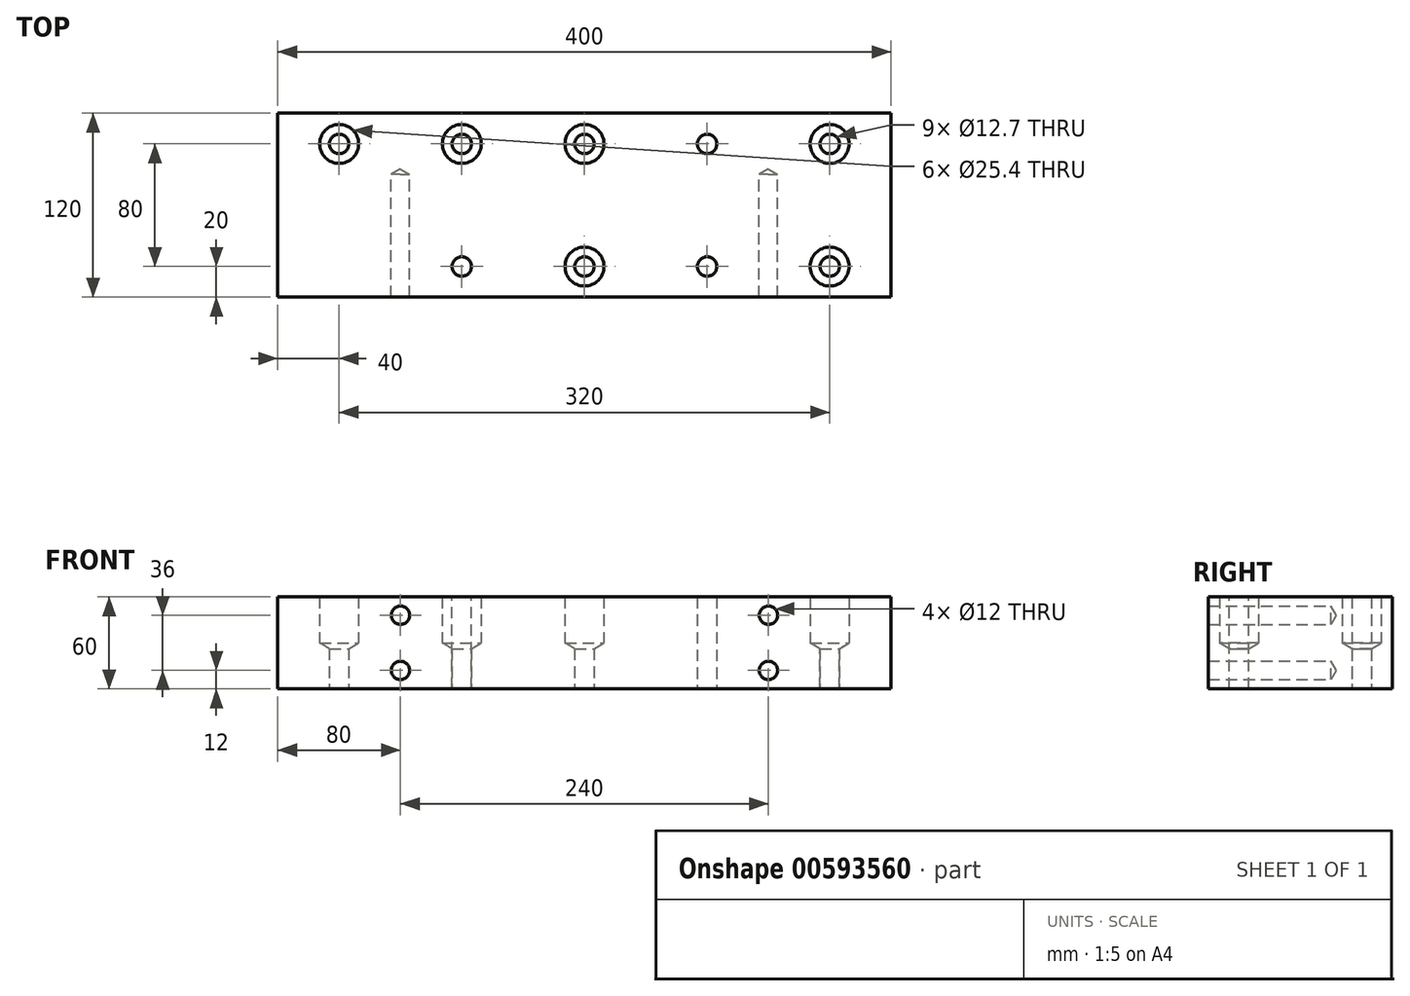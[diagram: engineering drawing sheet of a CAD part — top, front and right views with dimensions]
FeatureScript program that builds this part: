
annotation { "Feature Type Name" : "Feature", "Feature Type Description" : "" }
export const myFeature = defineFeature(function(context is Context, id is Id, definition is map)
    precondition{}
    {
        {
            var Q0;
            Q0=qCreatedBy(makeId("Top.planeOp"),FACE);
            var sketch = newSketch(context, id + "F0", { "sketchPlane" : qUnion([Q0])});
            skLineSegment(sketch, "E0.bottom", {"start": v(-200, 120) * mm, "end": v(200, 120) * mm});
            skLineSegment(sketch, "E0.top", {"start": v(-200, 0) * mm, "end": v(200, 0) * mm});
            skLineSegment(sketch, "E0.left", {"start": v(-200, 120) * mm, "end": v(-200, 0) * mm});
            skLineSegment(sketch, "E0.right", {"start": v(200, 120) * mm, "end": v(200, 0) * mm});
            skCircle(sketch, "E1.MirrorC", {"center": v(160, 20) * mm, "radius": 12.7 * mm});
            skCircle(sketch, "E2.MirrorC", {"center": v(80, 20) * mm, "radius": 12.7 * mm});
            skCircle(sketch, "E3.MirrorC", {"center": v(0, 20) * mm, "radius": 6.35 * mm});
            skCircle(sketch, "E4.MirrorC", {"center": v(-80, 20) * mm, "radius": 12.7 * mm});
            skCircle(sketch, "E5.MirrorC", {"center": v(-80, 20) * mm, "radius": 6.35 * mm});
            skCircle(sketch, "E6.MirrorC", {"center": v(0, 20) * mm, "radius": 12.7 * mm});
            skCircle(sketch, "E7.MirrorC", {"center": v(160, 20) * mm, "radius": 6.35 * mm});
            skCircle(sketch, "E8.MirrorC", {"center": v(80, 20) * mm, "radius": 6.35 * mm});
            skCircle(sketch, "E9.MirrorC", {"center": v(160, 100) * mm, "radius": 6.35 * mm});
            skCircle(sketch, "E10.MirrorC", {"center": v(160, 100) * mm, "radius": 12.7 * mm});
            skCircle(sketch, "E11.MirrorC", {"center": v(-160, 100) * mm, "radius": 6.35 * mm});
            skCircle(sketch, "E12.MirrorC", {"center": v(80, 100) * mm, "radius": 12.7 * mm});
            skCircle(sketch, "E13.MirrorC", {"center": v(80, 100) * mm, "radius": 6.35 * mm});
            skCircle(sketch, "E14.MirrorC", {"center": v(0, 100) * mm, "radius": 6.35 * mm});
            skCircle(sketch, "E15.MirrorC", {"center": v(-80, 100) * mm, "radius": 6.35 * mm});
            skCircle(sketch, "E16.MirrorC", {"center": v(0, 100) * mm, "radius": 12.7 * mm});
            skCircle(sketch, "E17.MirrorC", {"center": v(-80, 100) * mm, "radius": 12.7 * mm});
            skCircle(sketch, "E18.MirrorC", {"center": v(-160, 100) * mm, "radius": 12.7 * mm});
            skSolve(sketch);
        }
        {
            var Q0;
            Q0=makeQuery(id+"F0.imprint","IMPRINT",FACE,{"disambiguationData":[TD([[makeQuery(id+"F0.imprint","IMPRINT",EDGE,{"derivedFrom":sQuery(id+"F0.wireOp",EDGE,"E0.bottom")}),-1.0]])]});
            var Q1;
            Q1=makeQuery(id+"F0.imprint","IMPRINT",FACE,{"disambiguationData":[TD([[makeQuery(id+"F0.imprint","IMPRINT",EDGE,{"derivedFrom":sQuery(id+"F0.wireOp",EDGE,"E18.MirrorC")}),1.0]])]});
            var Q2;
            Q2=makeQuery(id+"F0.imprint","IMPRINT",FACE,{"disambiguationData":[TD([[makeQuery(id+"F0.imprint","IMPRINT",EDGE,{"derivedFrom":sQuery(id+"F0.wireOp",EDGE,"E11.MirrorC")}),1.0]])]});
            var Q3;
            Q3=makeQuery(id+"F0.imprint","IMPRINT",FACE,{"disambiguationData":[TD([[makeQuery(id+"F0.imprint","IMPRINT",EDGE,{"derivedFrom":sQuery(id+"F0.wireOp",EDGE,"E15.MirrorC")}),-1.0]])]});
            var Q4;
            Q4=makeQuery(id+"F0.imprint","IMPRINT",FACE,{"disambiguationData":[TD([[makeQuery(id+"F0.imprint","IMPRINT",EDGE,{"derivedFrom":sQuery(id+"F0.wireOp",EDGE,"E15.MirrorC")}),1.0]])]});
            var Q5;
            Q5=makeQuery(id+"F0.imprint","IMPRINT",FACE,{"disambiguationData":[TD([[makeQuery(id+"F0.imprint","IMPRINT",EDGE,{"derivedFrom":sQuery(id+"F0.wireOp",EDGE,"E14.MirrorC")}),-1.0]])]});
            var Q6;
            Q6=makeQuery(id+"F0.imprint","IMPRINT",FACE,{"disambiguationData":[TD([[makeQuery(id+"F0.imprint","IMPRINT",EDGE,{"derivedFrom":sQuery(id+"F0.wireOp",EDGE,"E14.MirrorC")}),1.0]])]});
            var Q7;
            Q7=makeQuery(id+"F0.imprint","IMPRINT",FACE,{"disambiguationData":[TD([[makeQuery(id+"F0.imprint","IMPRINT",EDGE,{"derivedFrom":sQuery(id+"F0.wireOp",EDGE,"E13.MirrorC")}),1.0]])]});
            var Q8;
            Q8=makeQuery(id+"F0.imprint","IMPRINT",FACE,{"disambiguationData":[TD([[makeQuery(id+"F0.imprint","IMPRINT",EDGE,{"derivedFrom":sQuery(id+"F0.wireOp",EDGE,"E12.MirrorC")}),1.0]])]});
            var Q9;
            Q9=makeQuery(id+"F0.imprint","IMPRINT",FACE,{"disambiguationData":[TD([[makeQuery(id+"F0.imprint","IMPRINT",EDGE,{"derivedFrom":sQuery(id+"F0.wireOp",EDGE,"E9.MirrorC")}),1.0]])]});
            var Q10;
            Q10=makeQuery(id+"F0.imprint","IMPRINT",FACE,{"disambiguationData":[TD([[makeQuery(id+"F0.imprint","IMPRINT",EDGE,{"derivedFrom":sQuery(id+"F0.wireOp",EDGE,"E9.MirrorC")}),-1.0]])]});
            var Q11;
            Q11=makeQuery(id+"F0.imprint","IMPRINT",FACE,{"disambiguationData":[TD([[makeQuery(id+"F0.imprint","IMPRINT",EDGE,{"derivedFrom":sQuery(id+"F0.wireOp",EDGE,"E8.MirrorC")}),-1.0]])]});
            var Q12;
            Q12=makeQuery(id+"F0.imprint","IMPRINT",FACE,{"disambiguationData":[TD([[makeQuery(id+"F0.imprint","IMPRINT",EDGE,{"derivedFrom":sQuery(id+"F0.wireOp",EDGE,"E8.MirrorC")}),1.0]])]});
            var Q13;
            Q13=makeQuery(id+"F0.imprint","IMPRINT",FACE,{"disambiguationData":[TD([[makeQuery(id+"F0.imprint","IMPRINT",EDGE,{"derivedFrom":sQuery(id+"F0.wireOp",EDGE,"E7.MirrorC")}),-1.0]])]});
            var Q14;
            Q14=makeQuery(id+"F0.imprint","IMPRINT",FACE,{"disambiguationData":[TD([[makeQuery(id+"F0.imprint","IMPRINT",EDGE,{"derivedFrom":sQuery(id+"F0.wireOp",EDGE,"E1.MirrorC")}),-1.0]])]});
            var Q15;
            Q15=makeQuery(id+"F0.imprint","IMPRINT",FACE,{"disambiguationData":[TD([[makeQuery(id+"F0.imprint","IMPRINT",EDGE,{"derivedFrom":sQuery(id+"F0.wireOp",EDGE,"E3.MirrorC")}),-1.0]])]});
            var Q16;
            Q16=makeQuery(id+"F0.imprint","IMPRINT",FACE,{"disambiguationData":[TD([[makeQuery(id+"F0.imprint","IMPRINT",EDGE,{"derivedFrom":sQuery(id+"F0.wireOp",EDGE,"E3.MirrorC")}),1.0]])]});
            var Q17;
            Q17=makeQuery(id+"F0.imprint","IMPRINT",FACE,{"disambiguationData":[TD([[makeQuery(id+"F0.imprint","IMPRINT",EDGE,{"derivedFrom":sQuery(id+"F0.wireOp",EDGE,"E5.MirrorC")}),-1.0]])]});
            var Q18;
            Q18=makeQuery(id+"F0.imprint","IMPRINT",FACE,{"disambiguationData":[TD([[makeQuery(id+"F0.imprint","IMPRINT",EDGE,{"derivedFrom":sQuery(id+"F0.wireOp",EDGE,"E4.MirrorC")}),-1.0]])]});
            extrude(context, id + "F1", {"entities" : qUnion([Q0, Q1, Q2, Q3, Q4, Q5, Q6, Q7, Q8, Q9, Q10, Q11, Q12, Q13, Q14, Q15, Q16, Q17, Q18]), "oppositeDirection" : true, "depth" : 60 * mm, "offsetDistance" : 25 * mm});
        }
        {
            var Q0;
            Q0=qCreatedBy(makeId("Front.planeOp"),FACE);
            var sketch = newSketch(context, id + "F2", { "sketchPlane" : qUnion([Q0])});
            skLineSegment(sketch, "E19.bottom", {"start": v(-200, 0) * mm, "end": v(200, 0) * mm});
            skLineSegment(sketch, "E19.top", {"start": v(-200, -60) * mm, "end": v(200, -60) * mm});
            skLineSegment(sketch, "E19.left", {"start": v(-200, 0) * mm, "end": v(-200, -60) * mm});
            skLineSegment(sketch, "E19.right", {"start": v(200, 0) * mm, "end": v(200, -60) * mm});
            skPoint(sketch, "E20", {"position": v(-120, -12) * mm});
            skPoint(sketch, "E21", {"position": v(-120, -48) * mm});
            skPoint(sketch, "E22", {"position": v(120, -48) * mm});
            skPoint(sketch, "E23", {"position": v(120, -12) * mm});
            skSolve(sketch);
        }
        {
            var Q0;
            Q0=sQuery(id+"F2.wireOp",VERTEX,"E20");
            var Q1;
            Q1=sQuery(id+"F2.wireOp",VERTEX,"E21");
            var Q2;
            Q2=sQuery(id+"F2.wireOp",VERTEX,"E22");
            var Q3;
            Q3=sQuery(id+"F2.wireOp",VERTEX,"E23");
            var Q4;
            Q4=makeQuery(id+"F1.opExtrude","SWEPT_BODY",BODY,{"disambiguationData":[OSD([sQuery(id+"F0.wireOp",EDGE,"E0.bottom"),sQuery(id+"F0.wireOp",EDGE,"E0.top"),sQuery(id+"F0.wireOp",EDGE,"E0.left"),sQuery(id+"F0.wireOp",EDGE,"E0.right"),sQuery(id+"F0.wireOp",EDGE,"E4.MirrorC"),sQuery(id+"F0.wireOp",EDGE,"E1.MirrorC"),sQuery(id+"F0.wireOp",EDGE,"E6.MirrorC"),sQuery(id+"F0.wireOp",EDGE,"E2.MirrorC"),sQuery(id+"F0.wireOp",EDGE,"E18.MirrorC"),sQuery(id+"F0.wireOp",EDGE,"E10.MirrorC"),sQuery(id+"F0.wireOp",EDGE,"E12.MirrorC"),sQuery(id+"F0.wireOp",EDGE,"E16.MirrorC"),sQuery(id+"F0.wireOp",EDGE,"E17.MirrorC")])]});
            hole(context, id + "F3", {"style" : HoleStyle.SIMPLE, "endStyle" : HoleEndStyle.BLIND, "holeDiameter" : 12 * mm, "majorDiameter" : 5 * mm, "holeDepth" : 80 * mm, "isTappedThrough" : true, "tappedDepth" : 20 * mm, "tapClearance" : 3, "startFromSketch" : true, "locations" : qUnion([Q0, Q1, Q2, Q3]), "scope" : qUnion([Q4])});
        }
        {
            var Q0;
            Q0=sQuery(id+"F0.wireOp",VERTEX,"E11.MirrorC.center");
            var Q1;
            Q1=sQuery(id+"F0.wireOp",VERTEX,"E15.MirrorC.center");
            var Q2;
            Q2=sQuery(id+"F0.wireOp",VERTEX,"E14.MirrorC.center");
            var Q3;
            Q3=sQuery(id+"F0.wireOp",VERTEX,"E12.MirrorC.center");
            var Q4;
            Q4=sQuery(id+"F0.wireOp",VERTEX,"E9.MirrorC.center");
            var Q5;
            Q5=sQuery(id+"F0.wireOp",VERTEX,"E1.MirrorC.center");
            var Q6;
            Q6=sQuery(id+"F0.wireOp",VERTEX,"E2.MirrorC.center");
            var Q7;
            Q7=sQuery(id+"F0.wireOp",VERTEX,"E3.MirrorC.center");
            var Q8;
            Q8=sQuery(id+"F0.wireOp",VERTEX,"E4.MirrorC.center");
            var Q9;
            Q9=makeQuery(id+"F1.opExtrude","SWEPT_BODY",BODY,{"disambiguationData":[OSD([sQuery(id+"F0.wireOp",EDGE,"E0.bottom"),sQuery(id+"F0.wireOp",EDGE,"E0.top"),sQuery(id+"F0.wireOp",EDGE,"E0.left"),sQuery(id+"F0.wireOp",EDGE,"E0.right"),sQuery(id+"F0.wireOp",EDGE,"E4.MirrorC"),sQuery(id+"F0.wireOp",EDGE,"E1.MirrorC"),sQuery(id+"F0.wireOp",EDGE,"E6.MirrorC"),sQuery(id+"F0.wireOp",EDGE,"E2.MirrorC"),sQuery(id+"F0.wireOp",EDGE,"E18.MirrorC"),sQuery(id+"F0.wireOp",EDGE,"E10.MirrorC"),sQuery(id+"F0.wireOp",EDGE,"E12.MirrorC"),sQuery(id+"F0.wireOp",EDGE,"E16.MirrorC"),sQuery(id+"F0.wireOp",EDGE,"E17.MirrorC")])]});
            hole(context, id + "F4", {"style" : HoleStyle.SIMPLE, "endStyle" : HoleEndStyle.BLIND, "holeDiameter" : 25.4 * mm, "majorDiameter" : 5 * mm, "holeDepth" : 30 * mm, "isTappedThrough" : true, "tappedDepth" : 20 * mm, "tapClearance" : 3, "locations" : qUnion([Q0, Q1, Q2, Q3, Q4, Q5, Q6, Q7, Q8]), "scope" : qUnion([Q9])});
        }
        {
            var Q0;
            Q0=sQuery(id+"F0.wireOp",VERTEX,"E4.MirrorC.center");
            var Q1;
            Q1=sQuery(id+"F0.wireOp",VERTEX,"E15.MirrorC.center");
            var Q2;
            Q2=sQuery(id+"F0.wireOp",VERTEX,"E11.MirrorC.center");
            var Q3;
            Q3=sQuery(id+"F0.wireOp",VERTEX,"E14.MirrorC.center");
            var Q4;
            Q4=sQuery(id+"F0.wireOp",VERTEX,"E3.MirrorC.center");
            var Q5;
            Q5=sQuery(id+"F0.wireOp",VERTEX,"E2.MirrorC.center");
            var Q6;
            Q6=sQuery(id+"F0.wireOp",VERTEX,"E12.MirrorC.center");
            var Q7;
            Q7=sQuery(id+"F0.wireOp",VERTEX,"E9.MirrorC.center");
            var Q8;
            Q8=sQuery(id+"F0.wireOp",VERTEX,"E1.MirrorC.center");
            var Q9;
            Q9=makeQuery(id+"F1.opExtrude","SWEPT_BODY",BODY,{"disambiguationData":[OSD([sQuery(id+"F0.wireOp",EDGE,"E0.bottom"),sQuery(id+"F0.wireOp",EDGE,"E0.top"),sQuery(id+"F0.wireOp",EDGE,"E0.left"),sQuery(id+"F0.wireOp",EDGE,"E0.right")])]});
            hole(context, id + "F5", {"style" : HoleStyle.SIMPLE, "endStyle" : HoleEndStyle.THROUGH, "holeDiameter" : 12.7 * mm, "majorDiameter" : 5 * mm, "isTappedThrough" : true, "tappedDepth" : 20 * mm, "tapClearance" : 3, "locations" : qUnion([Q0, Q1, Q2, Q3, Q4, Q5, Q6, Q7, Q8]), "scope" : qUnion([Q9])});
        }
    });
